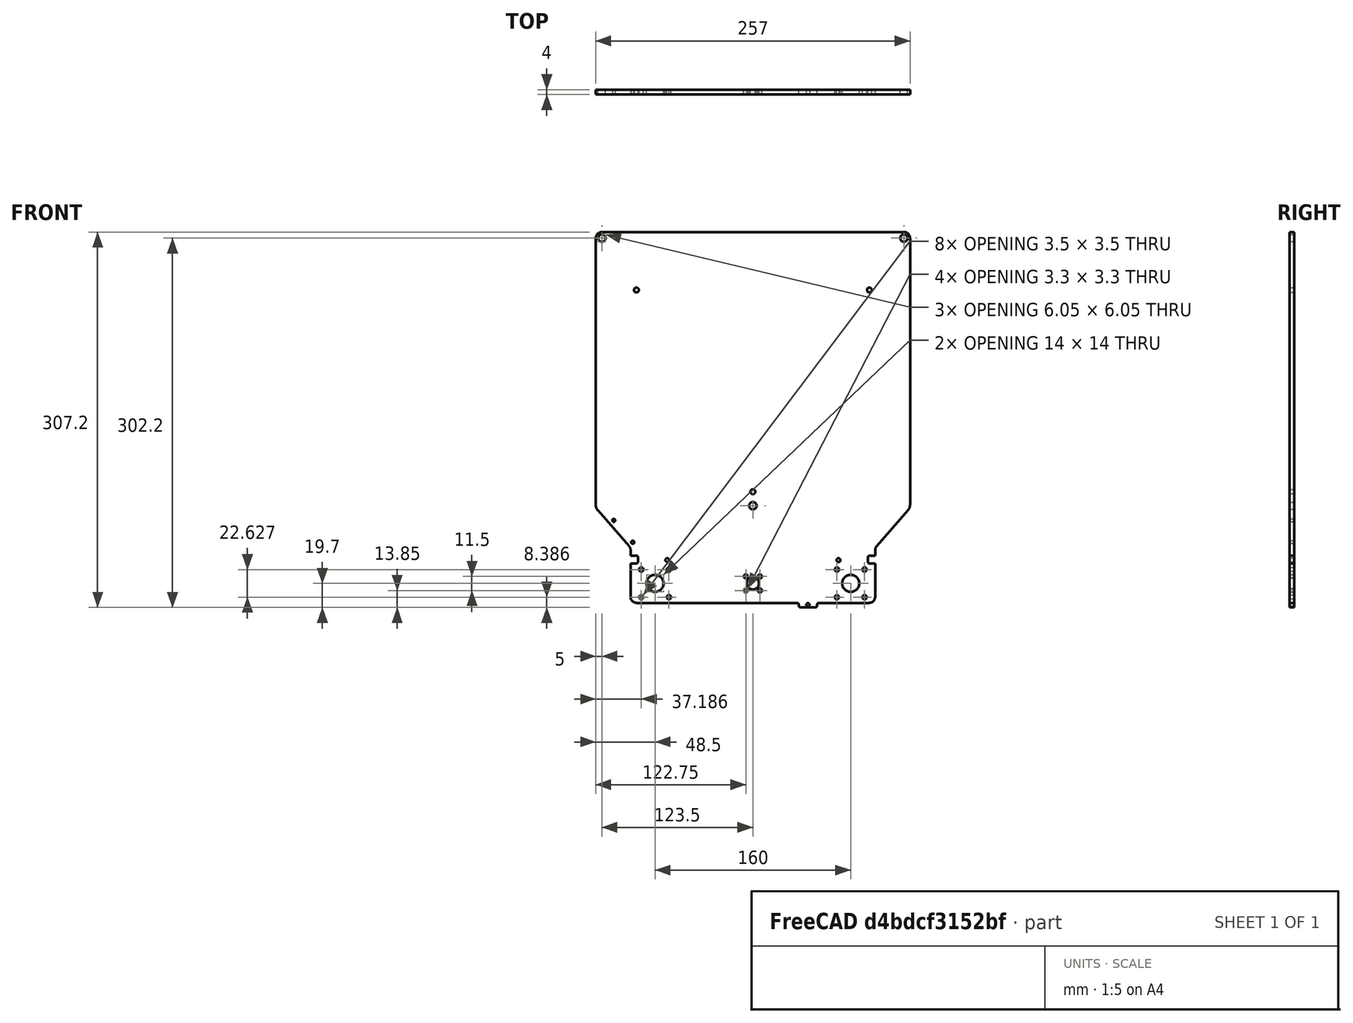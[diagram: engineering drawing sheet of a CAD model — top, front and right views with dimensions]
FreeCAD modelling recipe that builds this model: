
FCSTD DOCUMENT  (FreeCAD 0.16R5195 (Git))
Label: print-plate
License: All rights reserved
LicenseURL: https://ru.wikipedia.org/wiki/All_rights_reserved
objects: App::FeaturePython×3, Part::Feature×1, Sketcher::SketchObject×1, Drawing::FeaturePage×1, Part::Part2DObjectPython×1
note: 3 computed .brp shape members not serialized (recipe doc carries the construction recipe); baked Part::Feature solids carry a one-line shape summary decoded from their .brp

FEATURE [Part::Feature] Part__Feature  label="1"
  shape: bbox 257 x 4 x 307.2 mm, 90 faces (baked)
FEATURE [Sketcher::SketchObject] Sketch
  ExternalGeometry = -> [Part__Feature]
  Placement = pos=(0,0,0) rot=(1,0,0;1.5708rad)
  Support = -> Part__Feature [Face32]
  sketch-geometry (24):
    g0: LineSegment StartX=-100 StartY=-16 StartZ=0 EndX=-100 EndY=29 EndZ=0
    g1: LineSegment StartX=-100 StartY=29 StartZ=0 EndX=-128.439 EndY=62 EndZ=0
    g2: LineSegment StartX=-128.439 StartY=62 StartZ=0 EndX=-128.439 EndY=287 EndZ=0
    g3: LineSegment StartX=-128.439 StartY=287 StartZ=0 EndX=128.561 EndY=287 EndZ=0
    g4: LineSegment StartX=128.561 StartY=287 StartZ=0 EndX=128.561 EndY=61 EndZ=0
    g5: LineSegment StartX=128.561 StartY=61 StartZ=0 EndX=100 EndY=29 EndZ=0
    g6: LineSegment StartX=100 StartY=29 StartZ=0 EndX=100 EndY=22.6847 EndZ=0
    g7: LineSegment StartX=100 StartY=22.5015 StartZ=0 EndX=100 EndY=-16 EndZ=0
    g8: LineSegment StartX=100 StartY=-16 StartZ=0 EndX=-100 EndY=-16 EndZ=0
    g9: Circle CenterX=80 CenterY=0 CenterZ=0 NormalX=0 NormalY=0 NormalZ=1 Radius=7
    g10: Circle CenterX=68.6658 CenterY=11.3138 CenterZ=0 NormalX=0 NormalY=0 NormalZ=1 Radius=1.75
    g11: Circle CenterX=68.6863 CenterY=-11.3137 CenterZ=0 NormalX=0 NormalY=0 NormalZ=1 Radius=1.75
    g12: Circle CenterX=91.3137 CenterY=11.3137 CenterZ=0 NormalX=0 NormalY=0 NormalZ=1 Radius=1.75
    g13: Circle CenterX=91.3137 CenterY=-11.3137 CenterZ=0 NormalX=0 NormalY=0 NormalZ=1 Radius=1.75
    g14: Circle CenterX=-80 CenterY=0 CenterZ=0 NormalX=0 NormalY=0 NormalZ=1 Radius=7
    g15: Circle CenterX=-91.3137 CenterY=11.3137 CenterZ=0 NormalX=0 NormalY=0 NormalZ=1 Radius=1.75
    g16: Circle CenterX=-91.3137 CenterY=-11.3137 CenterZ=0 NormalX=0 NormalY=0 NormalZ=1 Radius=1.75
    g17: Circle CenterX=-68.6863 CenterY=11.3137 CenterZ=0 NormalX=0 NormalY=0 NormalZ=1 Radius=1.75
    g18: Circle CenterX=-68.714 CenterY=-11.3312 CenterZ=0 NormalX=0 NormalY=0 NormalZ=1 Radius=1.76766
    g19: Circle CenterX=0 CenterY=-0.1 CenterZ=0 NormalX=0 NormalY=0 NormalZ=1 Radius=5
    g20: Circle CenterX=5.75 CenterY=5.65 CenterZ=0 NormalX=0 NormalY=0 NormalZ=1 Radius=1.65
    g21: Circle CenterX=5.75 CenterY=-5.85 CenterZ=0 NormalX=0 NormalY=0 NormalZ=1 Radius=1.65
    g22: Circle CenterX=-5.75 CenterY=5.65 CenterZ=0 NormalX=0 NormalY=0 NormalZ=1 Radius=1.65
    g23: Circle CenterX=-5.75 CenterY=-5.85 CenterZ=0 NormalX=0 NormalY=0 NormalZ=1 Radius=1.65
  constraints (52):
    c: Vertical(g0)
    c: Coincident(g1,g0)
    c: Coincident(g1,g2)
    c: Vertical(g2)
    c: Coincident(g2,g3)
    c: Horizontal(g3)
    c: Coincident(g3,g4)
    c: Vertical(g4)
    c: Coincident(g4,g5)
    c: Coincident(g5,g6)
    c: Vertical(g6)
    c: Vertical(g7)
    c: Coincident(g7,g8)
    c: Coincident(g8,g0)
    c: Horizontal(g8)
    c: PointOnObject(g-10,g9)
    c: PointOnObject(g-11,g10)
    c: Coincident(g11,g-12)
    c: PointOnObject(g-12,g11)
    c: Radius(g9) = 7
    c: Radius(g10) = 1.75
    c: DistanceY(g-22,g-21) = 22.6274
    c: Distance(g9,g-21) = 16
    c: Coincident(g12,g-21)
    c: PointOnObject(g-21,g12)
    c: Coincident(g13,g-22)
    c: PointOnObject(g-22,g13)
    c: Coincident(g14,g-8)
    c: PointOnObject(g-8,g14)
    c: Coincident(g15,g-14)
    c: PointOnObject(g-14,g15)
    c: Coincident(g16,g-15)
    c: PointOnObject(g-15,g16)
    c: PointOnObject(g-23,g17)
    c: PointOnObject(g-24,g18)
    c: Coincident(g19,g-9)
    c: PointOnObject(g-9,g19)
    c: Coincident(g20,g-25)
    c: PointOnObject(g-25,g20)
    c: Coincident(g21,g-26)
    c: PointOnObject(g-26,g21)
    c: Coincident(g22,g-13)
    c: PointOnObject(g-13,g22)
    c: Coincident(g23,g-16)
    c: PointOnObject(g-16,g23)
    c: DistanceY(g14,g0) = -16
    c: DistanceX(g14,g0) = -20
    c: DistanceX(g0,g7) = 200
    c: DistanceX(g3,g2) = -257
    c: DistanceY(g7,g3) = 303
    c: DistanceY(g5,g7) = -45
    c: DistanceY(g7,g4) = 77
FEATURE [Drawing::FeaturePage] Page
FEATURE [Part::Part2DObjectPython] DWire  # Draft 2D object (typed FeaturePython)
  ChamferSize = 0
  Closed = true
  End = (-130,0,60)
  FilletRadius = 0
  Length = 1096.85
  MakeFace = true
  Points = (8) [(-130,0,290),(130,0,290),(130,0,60),(100,0,30),(100,-3.55271e-15,-16),(-100,-3.55271e-15,-16),(-100,0,30),(-130,0,60)]
  Start = (-130,0,290)
FEATURE [App::FeaturePython] Dimension  # Draft dimension (typed FeaturePython)
  Dimline = (100,0,-69.1978)
  Direction = (0,0,0)
  Distance = 200
  End = (100,0,-16)
  Normal = (0,-1,5.9605e-08)
  Start = (-100,0,-16)
FEATURE [App::FeaturePython] Dimension001  # Draft dimension (typed FeaturePython)
  Dimline = (-242.815,0,159.523)
  Direction = (0,0,0)
  Distance = 306
  End = (-100,0,290)
  Normal = (0,-1,0)
  Start = (-100,0,-16)
FEATURE [App::FeaturePython] Dimension002  # Draft dimension (typed FeaturePython)
  Dimline = (-169.764,0,30)
  Direction = (0,0,0)
  Distance = 46
  End = (-100,0,30)
  Normal = (0,-1,0)
  Start = (-100,0,-16)
